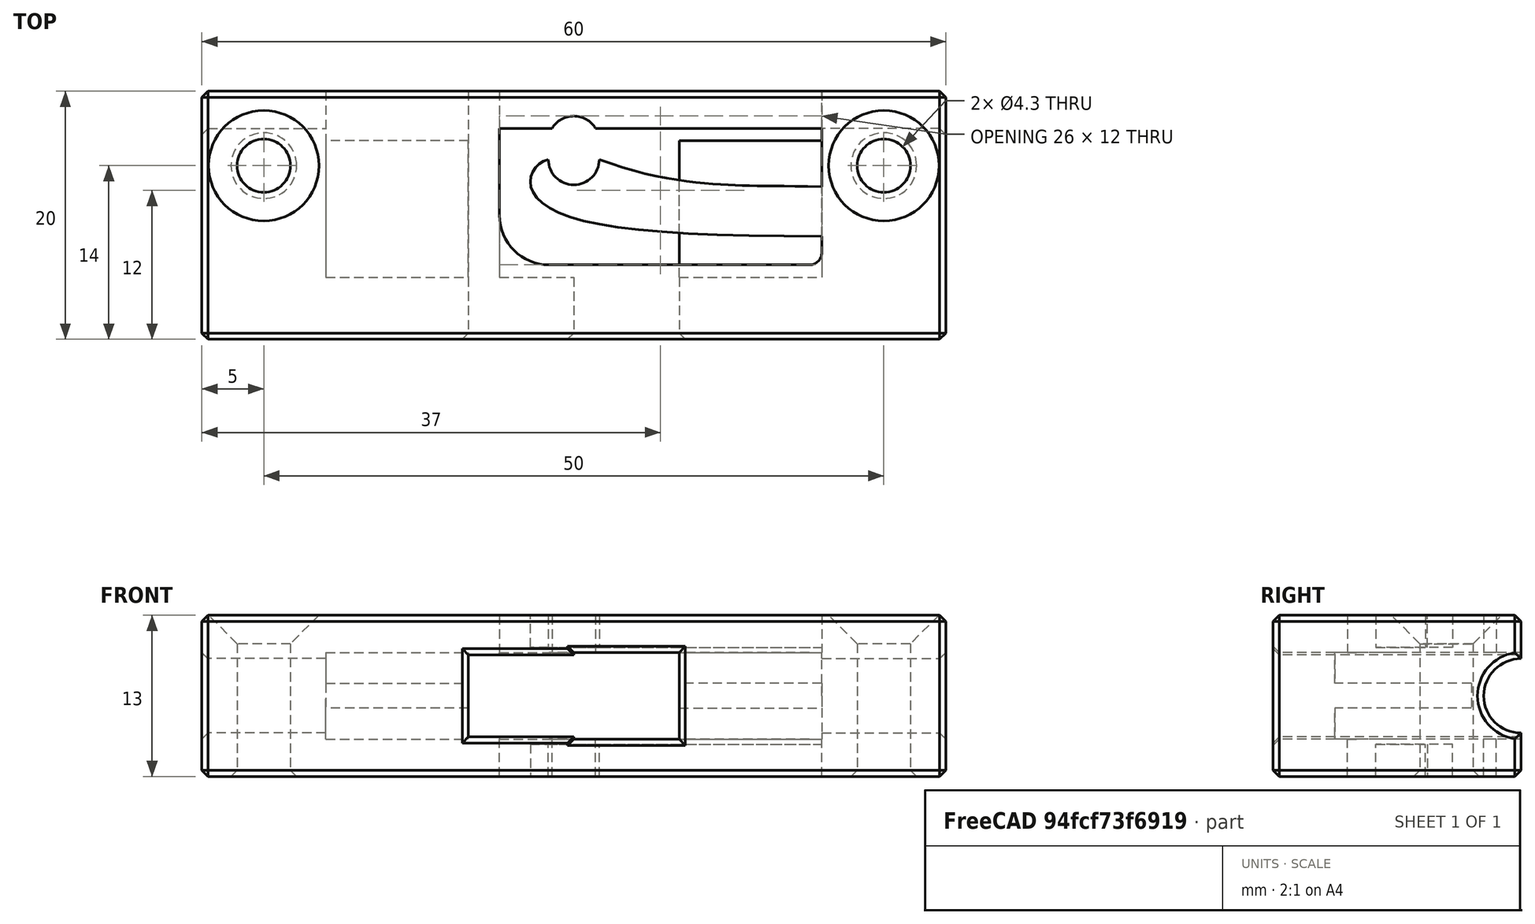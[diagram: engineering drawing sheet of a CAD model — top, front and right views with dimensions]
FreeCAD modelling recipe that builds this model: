
FCSTD DOCUMENT  (FreeCAD 1.1R20260414 (Git shallow))
Label: 01_hanger
License: All rights reserved
LicenseURL: http://en.wikipedia.org/wiki/All_rights_reserved
objects: Sketcher::SketchObject×8, PartDesign::Pocket×6, TechDraw::DrawProjGroupItem×6, PartDesign::Pad×2, PartDesign::Chamfer×2, TechDraw::DrawViewDimension×2, TechDraw::DrawSVGTemplate×1, PartDesign::Mirrored×1, App::Point×1, PartDesign::Body×1, TechDraw::DrawProjGroup×1, TechDraw::DrawViewSection×1, TechDraw::DrawPage×1
note: 52 computed .brp shape members not serialized (recipe doc carries the construction recipe); baked Part::Feature solids carry a one-line shape summary decoded from their .brp

FEATURE [Sketcher::SketchObject] Sketch
  ArcFitTolerance = 1e-06
  AttachmentSupport = -> [XY_Plane]
  ExternalTypes = [0]
  FullyConstrained = true
  MakeInternals = false
  MapMode = 5
  _ExternalGeoVersion = 0
  sketch-geometry (5):
    g0: LineSegment StartX=-30 StartY=10 StartZ=0 EndX=-30 EndY=-10 EndZ=0
    g1: LineSegment StartX=-30 StartY=-10 StartZ=0 EndX=30 EndY=-10 EndZ=0
    g2: LineSegment StartX=30 StartY=-10 StartZ=0 EndX=30 EndY=10 EndZ=0
    g3: LineSegment StartX=30 StartY=10 StartZ=0 EndX=-30 EndY=10 EndZ=0
    g4: LineSegment [constr] StartX=-30 StartY=10 StartZ=0 EndX=30 EndY=-10 EndZ=0
  constraints (13):
    c: Coincident(g0,g1)
    c: Coincident(g1,g2)
    c: Coincident(g2,g3)
    c: Coincident(g3,g0)
    c: Vertical(g0)
    c: Vertical(g2)
    c: Horizontal(g1)
    c: Horizontal(g3)
    c: Coincident(g4,g0)
    c: Coincident(g4,g1)
    c: Symmetric(g4,g4,g-1)
    c: DistanceX(g3,g3) = 60
    c: DistanceY(g0,g0) = 20
FEATURE [PartDesign::Pad] Pad
  Direction = (0,0,1)
  Length = 6.5
  Length2 = 10
  Profile = -> Sketch
  ReferenceAxis = -> Sketch [N_Axis]
  SideType = 0
  Suppressed = false
  Type = 0
  Type2 = 0
FEATURE [Sketcher::SketchObject] Sketch001
  ArcFitTolerance = 1e-06
  AttachmentSupport = -> [YZ_Plane]
  ExternalGeometry = -> [Pad]
  ExternalTypes = [0]
  FullyConstrained = true
  MakeInternals = false
  MapMode = 5
  Placement = pos=(0,0,0) rot=(0.57735,0.57735,0.57735;2.0944rad)
  _ExternalGeoVersion = 0
  sketch-geometry (3):
    g0: ArcOfCircle CenterX=10 CenterY=0 CenterZ=0 NormalX=0 NormalY=0 NormalZ=1 AngleXU=0 Radius=3 StartAngle=1.5708 EndAngle=3.14159
    g1: LineSegment StartX=7 StartY=4e-16 StartZ=0 EndX=10 EndY=0 EndZ=0
    g2: LineSegment StartX=10 StartY=0 StartZ=0 EndX=10 EndY=3 EndZ=0
  constraints (8):
    c: Coincident(g0,g-4)
    c: PointOnObject(g0,g-4)
    c: PointOnObject(g0,g-3)
    c: Radius(g0) = 3
    c: Coincident(g1,g0)
    c: Coincident(g1,g0)
    c: Coincident(g2,g0)
    c: Coincident(g2,g0)
FEATURE [PartDesign::Pocket] Pocket
  BaseFeature = -> Pad
  Direction = (-1,0,0)
  Length = 5
  Length2 = 5
  Profile = -> Sketch001
  ReferenceAxis = -> Sketch001 [N_Axis]
  SideType = 2
  Suppressed = false
  Type = 1
  Type2 = 0
FEATURE [Sketcher::SketchObject] Sketch002
  ArcFitTolerance = 1e-06
  AttachmentSupport = -> [XY_Plane]
  ExternalTypes = [0]
  FullyConstrained = true
  MakeInternals = false
  MapMode = 5
  _ExternalGeoVersion = 0
  sketch-geometry (4):
    g0: Circle CenterX=0 CenterY=5.95 CenterZ=0 NormalX=0 NormalY=0 NormalZ=1 AngleXU=0 Radius=2.05
    g1: LineSegment [constr] StartX=25 StartY=4 StartZ=0 EndX=-25 EndY=4 EndZ=0
    g2: Circle CenterX=25 CenterY=4 CenterZ=0 NormalX=0 NormalY=0 NormalZ=1 AngleXU=0 Radius=2.15
    g3: Circle CenterX=-25 CenterY=4 CenterZ=0 NormalX=0 NormalY=0 NormalZ=1 AngleXU=0 Radius=2.15
  constraints (11):
    c: PointOnObject(g0,g-2)
    c: Diameter(g0) = 4.1
    c: Distance(g0,g-3) = 4.05
    c: Horizontal(g1)
    c: Coincident(g2,g1)
    c: Coincident(g3,g1)
    c: Diameter(g2) = 4.3
    c: Diameter(g3) = 4.3
    c: DistanceX(g1,g1) = 50
    c: Distance(g1,g-3) = 6
    c: DistanceX(g-3,g1) = 5
FEATURE [PartDesign::Pocket] Pocket001
  BaseFeature = -> Pocket
  Direction = (0,0,-1)
  Length = 5
  Length2 = 5
  Profile = -> Sketch002
  ReferenceAxis = -> Sketch002 [N_Axis]
  SideType = 2
  Suppressed = false
  Type = 1
  Type2 = 0
FEATURE [Sketcher::SketchObject] Sketch003
  ArcFitTolerance = 1e-06
  AttachmentOffset = pos=(0,0,6.5) rot=(0,0,1;0rad)
  AttachmentSupport = -> [XY_Plane]
  ExternalGeometry = -> [Pocket001]
  ExternalTypes = [0]
  FullyConstrained = true
  MakeInternals = false
  MapMode = 5
  Placement = pos=(0,0,6.5) rot=(0,0,1;0rad)
  _ExternalGeoVersion = 0
  sketch-geometry (8):
    g0: LineSegment StartX=20 StartY=7 StartZ=0 EndX=-6 EndY=7 EndZ=0
    g1: LineSegment StartX=-6 StartY=7 StartZ=0 EndX=-6 EndY=0 EndZ=0
    g2: LineSegment StartX=-2 StartY=-4 StartZ=0 EndX=19 EndY=-4 EndZ=0
    g3: LineSegment StartX=20 StartY=-3 StartZ=0 EndX=20 EndY=7 EndZ=0
    g4: ArcOfCircle CenterX=-2 CenterY=-6e-16 CenterZ=0 NormalX=0 NormalY=0 NormalZ=1 AngleXU=0 Radius=4 StartAngle=3.14159 EndAngle=4.71239
    g5: GeomPoint [constr] X=-6 Y=-4 Z=0
    g6: ArcOfCircle CenterX=19 CenterY=-3 CenterZ=0 NormalX=0 NormalY=0 NormalZ=1 AngleXU=0 Radius=1 StartAngle=4.71239 EndAngle=6.28319
    g7: GeomPoint [constr] X=20 Y=-4 Z=0
  constraints (20):
    c: Coincident(g0,g1)
    c: Coincident(g3,g0)
    c: Horizontal(g0)
    c: Horizontal(g2)
    c: Vertical(g1)
    c: Vertical(g3)
    c: Distance(g7,g-3) = 10
    c: Distance(g-4,g0) = 3
    c: DistanceY(g5,g1) = 11
    c: PointOnObject(g5,g2)
    c: PointOnObject(g5,g1)
    c: Tangent(g2,g4) = -1.5708
    c: Tangent(g1,g4) = -1.5708
    c: Radius(g4) = 4
    c: DistanceX(g0,g0) = 26
    c: PointOnObject(g7,g2)
    c: PointOnObject(g7,g3)
    c: Tangent(g2,g6) = -1.5708
    c: Tangent(g3,g6) = -1.5708
    c: Radius(g6) = 1
FEATURE [PartDesign::Pocket] Pocket002
  BaseFeature = -> Pocket001
  Direction = (0,0,-1)
  Length = 4
  Length2 = 5
  Profile = -> Sketch003
  ReferenceAxis = -> Sketch003 [N_Axis]
  SideType = 0
  Suppressed = false
  Type = 0
  Type2 = 0
FEATURE [Sketcher::SketchObject] Sketch004
  ArcFitTolerance = 1e-06
  AttachmentOffset = pos=(0,0,-10) rot=(0,0,1;0rad)
  AttachmentSupport = -> [XZ_Plane]
  ExternalGeometry = -> [Pocket002]
  ExternalTypes = [0]
  FullyConstrained = false
  MakeInternals = false
  MapMode = 5
  Placement = pos=(0,10,-2.2e-15) rot=(1,0,0;1.5708rad)
  _ExternalGeoVersion = 0
  sketch-geometry (8):
    g0: LineSegment StartX=-20 StartY=1 StartZ=0 EndX=20 EndY=1 EndZ=0
    g1: LineSegment StartX=20 StartY=1 StartZ=0 EndX=20 EndY=3.5 EndZ=0
    g2: LineSegment StartX=-20 StartY=3.5 StartZ=0 EndX=-20 EndY=1 EndZ=0
    g3: LineSegment StartX=-20 StartY=3.5 StartZ=0 EndX=-8.5 EndY=3.5 EndZ=0
    g4: LineSegment StartX=-8.5 StartY=3.5 StartZ=0 EndX=-8.5 EndY=3.3 EndZ=0
    g5: LineSegment StartX=-8.5 StartY=3.3 StartZ=0 EndX=-6 EndY=3.3 EndZ=0
    g6: LineSegment StartX=-6 StartY=3.3 StartZ=0 EndX=-6 EndY=3.5 EndZ=0
    g7: LineSegment StartX=-6 StartY=3.5 StartZ=0 EndX=20 EndY=3.5 EndZ=0
  constraints (23):
    c: Coincident(g0,g1)
    c: Coincident(g2,g0)
    c: Horizontal(g0)
    c: Vertical(g1)
    c: Vertical(g2)
    c: DistanceX(g0,g0) = 40
    c: Coincident(g3,g2)
    c: Horizontal(g3)
    c: Coincident(g4,g3)
    c: Coincident(g5,g4)
    c: Vertical(g4)
    c: Horizontal(g5)
    c: Coincident(g6,g5)
    c: Vertical(g6)
    c: Coincident(g7,g6)
    c: Coincident(g7,g1)
    c: Horizontal(g7)
    c: Equal(g4,g6)
    c: Distance(g4,g4) = 0.2
    c: Distance(g1,g1) = 2.5
    c: Distance(g0,g-2) = 20
    c: DistanceX(g2,g3) = 11.5
    c: Distance(g5,g5) = 2.5
FEATURE [PartDesign::Pocket] Pocket003
  BaseFeature = -> Pocket002
  Direction = (0,1,-2e-16)
  Length = 15
  Length2 = 5
  Profile = -> Sketch004
  ReferenceAxis = -> Sketch004 [N_Axis]
  Reversed = true
  SideType = 0
  Suppressed = false
  Type = 0
  Type2 = 0
FEATURE [Sketcher::SketchObject] Sketch005
  ArcFitTolerance = 1e-06
  AttachmentSupport = -> [XZ_Plane]
  ExternalTypes = [0]
  FullyConstrained = true
  MakeInternals = false
  MapMode = 5
  Placement = pos=(0,0,0) rot=(1,0,0;1.5708rad)
  _ExternalGeoVersion = 0
  sketch-geometry (6):
    g0: LineSegment StartX=-8.5 StartY=3.3 StartZ=0 EndX=-8.5 EndY=0 EndZ=0
    g1: LineSegment StartX=-8.5 StartY=0 StartZ=0 EndX=8.5 EndY=0 EndZ=0
    g2: LineSegment StartX=8.5 StartY=0 StartZ=0 EndX=8.5 EndY=3.5 EndZ=0
    g3: LineSegment StartX=8.5 StartY=3.5 StartZ=0 EndX=0 EndY=3.5 EndZ=0
    g4: LineSegment StartX=0 StartY=3.5 StartZ=0 EndX=0 EndY=3.3 EndZ=0
    g5: LineSegment StartX=-8.5 StartY=3.3 StartZ=0 EndX=0 EndY=3.3 EndZ=0
  constraints (18):
    c: Coincident(g0,g1)
    c: Coincident(g1,g2)
    c: Coincident(g2,g3)
    c: Vertical(g0)
    c: Vertical(g2)
    c: Horizontal(g1)
    c: Horizontal(g3)
    c: PointOnObject(g1,g-1)
    c: Distance(g-1,g2) = 8.5
    c: Distance(g2,g2) = 3.5
    c: Coincident(g5,g4)
    c: Horizontal(g5)
    c: Coincident(g0,g5)
    c: PointOnObject(g4,g-2)
    c: Distance(g-2,g0) = 8.5
    c: Coincident(g4,g3)
    c: Distance(g3,g5) = 0.2
    c: Vertical(g4)
FEATURE [PartDesign::Pocket] Pocket004
  BaseFeature = -> Pocket003
  Direction = (0,1,-2e-16)
  Length = 5
  Length2 = 5
  Profile = -> Sketch005
  ReferenceAxis = -> Sketch005 [N_Axis]
  SideType = 2
  Suppressed = false
  Type = 1
  Type2 = 0
FEATURE [Sketcher::SketchObject] Sketch006
  ArcFitTolerance = 1e-06
  AttachmentOffset = pos=(0,0,6.5) rot=(0,0,1;0rad)
  AttachmentSupport = -> [XY_Plane]
  ExternalGeometry = -> [Pocket004]
  ExternalTypes = [0]
  FullyConstrained = false
  MakeInternals = false
  MapMode = 5
  Placement = pos=(0,0,6.5) rot=(0,0,1;0rad)
  _ExternalGeoVersion = 0
  sketch-geometry (20):
    g0: ArcOfCircle CenterX=0 CenterY=4.5 CenterZ=0 NormalX=0 NormalY=0 NormalZ=1 AngleXU=0 Radius=2.05 StartAngle=3.14159 EndAngle=6.28319
    g1: LineSegment [constr] StartX=-2.05 StartY=4.5 StartZ=0 EndX=2.05 EndY=4.5 EndZ=0
    g2-g5: Circle [constr] x4 (B-spline internal-alignment scaffolding for g6; pole/knot coordinates omitted)
    g6: BSplineCurve PolesCount=5 KnotsCount=2 Degree=4 IsPeriodic=0
    g7: GeomPoint [constr] X=-2.05 Y=4.5 Z=0
    g8: GeomPoint [constr] X=20 Y=-1.7 Z=0
    g9-g13: Circle [constr] x5 (B-spline internal-alignment scaffolding for g14; pole/knot coordinates omitted)
    g14: BSplineCurve PolesCount=5 KnotsCount=3 Degree=3 IsPeriodic=0
    g15: GeomPoint [constr] X=2.05 Y=4.5 Z=0
    g16: GeomPoint [constr] X=11.5418 Y=2.50077 Z=0
    g17: GeomPoint [constr] X=20 Y=2.3 Z=0
    g18: Circle [constr] CenterX=20 CenterY=-1.7 CenterZ=0 NormalX=0 NormalY=0 NormalZ=1 AngleXU=0 Radius=1
    g19: LineSegment StartX=20 StartY=-1.7 StartZ=0 EndX=20 EndY=2.3 EndZ=0
  constraints (30):
    c: PointOnObject(g0,g-2)
    c: Diameter(g0) = 4.1
    c: Distance(g0,g-4) = 5.5
    c: Horizontal(g1)
    c: PointOnObject(g0,g1)
    c: Coincident(g0,g1)
    c: Coincident(g0,g1)
    c: PointOnObject(g13,g-3)
    c: Weight(g2) = 1
    c: Equal(g2,g3)
    c: Equal(g2,g4)
    c: Equal(g2,g5)
    c: InternalAlignment(g2-g5 -> g6) x4
    c: InternalAlignment(g7,g6)
    c: InternalAlignment(g8,g6)
    c: Weight(g9) = 1
    c: Equal(g9, g10-g13) x4
    c: InternalAlignment(g9-g13 -> g14) x5
    c: InternalAlignment(g15,g14)
    c: InternalAlignment(g16,g14)
    c: InternalAlignment(g17,g14)
    c: Coincident(g9,g0)
    c: Coincident(g6,g0)
    c: PointOnObject(g6,g-3)
    c: DistanceY(g6,g14) = 4
    c: Distance(g6,g-5) = 2.3
    c: InternalAlignment(g18,g6)
    c: Equal(g18,g2)
    c: Coincident(g19,g6)
    c: Coincident(g19,g14)
FEATURE [PartDesign::Pad] Pad001
  BaseFeature = -> Pocket004
  Direction = (0,0,1)
  Length = 2.6
  Length2 = 10
  Profile = -> Sketch006
  ReferenceAxis = -> Sketch006 [N_Axis]
  Refine = true
  Reversed = true
  SideType = 0
  Suppressed = false
  Type = 0
  Type2 = 0
FEATURE [TechDraw::DrawSVGTemplate] Template
  Height = 210
  Orientation = 1
  Template = C:/Program Files/FreeCAD 1.0/data/Mod/TechDraw/Templates/Default_Template_A4_Landscape.svg
  Width = 297
FEATURE [Sketcher::SketchObject] Sketch007
  ArcFitTolerance = 1e-06
  AttachmentOffset = pos=(0,0,-10) rot=(0,0,1;0rad)
  AttachmentSupport = -> [XZ_Plane]
  ExternalGeometry = -> [Pad001]
  ExternalTypes = [0]
  FullyConstrained = true
  MakeInternals = false
  MapMode = 5
  Placement = pos=(0,10,-2.2e-15) rot=(1,0,0;1.5708rad)
  _ExternalGeoVersion = 0
  sketch-geometry (4):
    g0: LineSegment StartX=-20 StartY=3 StartZ=0 EndX=-20 EndY=1.8e-15 EndZ=0
    g1: LineSegment StartX=-20 StartY=1.8e-15 StartZ=0 EndX=20 EndY=1.8e-15 EndZ=0
    g2: LineSegment StartX=20 StartY=1.8e-15 StartZ=0 EndX=20 EndY=3 EndZ=0
    g3: LineSegment StartX=20 StartY=3 StartZ=0 EndX=-20 EndY=3 EndZ=0
  constraints (11):
    c: Coincident(g0,g1)
    c: Coincident(g1,g2)
    c: Coincident(g2,g3)
    c: Coincident(g3,g0)
    c: Vertical(g0)
    c: Vertical(g2)
    c: Horizontal(g1)
    c: Horizontal(g3)
    c: Coincident(g0,g-3)
    c: DistanceX(g3,g3) = 40
    c: DistanceY(g0,g0) = 3
FEATURE [PartDesign::Pocket] Pocket005
  BaseFeature = -> Pad001
  Direction = (0,1,-2e-16)
  Length = 4
  Length2 = 5
  Profile = -> Sketch007
  ReferenceAxis = -> Sketch007 [N_Axis]
  Reversed = true
  SideType = 0
  Suppressed = false
  Type = 0
  Type2 = 0
FEATURE [PartDesign::Mirrored] Mirrored
  BaseFeature = -> Pocket005
  MirrorPlane = -> XY_Plane
  Refine = true
  Suppressed = false
  TransformMode = 1
FEATURE [PartDesign::Chamfer] Chamfer001
  Angle = 45
  Base = -> Mirrored [Edge108,Edge107]
  BaseFeature = -> Mirrored
  ChamferType = 0
  FlipDirection = false
  Size = 2.3
  Size2 = 1
  SupportTransform = false
  Suppressed = false
  UseAllEdges = false
FEATURE [App::Point] Origin001  label="Origin"
  Role = Origin
FEATURE [PartDesign::Chamfer] Chamfer
  Angle = 45
  Base = -> Chamfer001 [Edge2,Edge5,Edge3,Edge4,Edge28,Edge27,Edge25,Edge39,Edge114,Edge24,Edge126,Edge102,Edge21,Edge37,Edge40,Edge38,Edge26,Edge23,Edge29,Edge31,Edge32,Edge33,Edge34,Edge35,Edge36,Edge30]
  BaseFeature = -> Chamfer001
  ChamferType = 0
  FlipDirection = false
  Refine = true
  Size = 0.5
  Size2 = 1
  SupportTransform = false
  Suppressed = false
  UseAllEdges = false
FEATURE [PartDesign::Body] Body
  AllowCompound = false
  Group = -> [Sketch,Pad,Sketch001,Pocket,Sketch002,Pocket001,Sketch003,Pocket002,Sketch004,Pocket003,Sketch005,Pocket004,Sketch006,Pad001,Sketch007,Pocket005,Mirrored,Chamfer001,Chamfer]
  Origin = -> Origin
  Tip = -> Chamfer
FEATURE [TechDraw::DrawProjGroupItem] View  label="Front"
  CoarseView = false
  Direction = (0,-1,0)
  Focus = 100
  HardHidden = false
  IsoCount = 0
  IsoHidden = false
  IsoVisible = false
  LockPosition = true
  Perspective = false
  Rotation = 0
  RotationVector = (1,0,0)
  ScaleType = 2
  ScrubCount = 1
  SeamHidden = false
  SeamVisible = true
  SmoothHidden = false
  SmoothVisible = true
  Source = -> [Body]
  Type = 0
  X = 0
  XDirection = (1,0,0)
  Y = 0
FEATURE [TechDraw::DrawProjGroupItem] ProjItem  label="Right"
  CoarseView = false
  Direction = (1,-1e-16,0)
  Focus = 100
  HardHidden = false
  IsoCount = 0
  IsoHidden = false
  IsoVisible = false
  LockPosition = false
  Perspective = false
  Rotation = 0
  RotationVector = (1,0,0)
  ScaleType = 0
  ScrubCount = 1
  SeamHidden = false
  SeamVisible = true
  SmoothHidden = false
  SmoothVisible = true
  Source = -> [Body]
  Type = 2
  X = 55
  XDirection = (1e-16,1,0)
  Y = 0
FEATURE [TechDraw::DrawProjGroupItem] ProjItem001  label="Left"
  CoarseView = false
  Direction = (-1,-1e-16,0)
  Focus = 100
  HardHidden = false
  IsoCount = 0
  IsoHidden = false
  IsoVisible = false
  LockPosition = false
  Perspective = false
  Rotation = 0
  RotationVector = (1,0,0)
  ScaleType = 0
  ScrubCount = 1
  SeamHidden = false
  SeamVisible = true
  SmoothHidden = false
  SmoothVisible = true
  Source = -> [Body]
  Type = 1
  X = -55
  XDirection = (1e-16,-1,0)
  Y = 0
FEATURE [TechDraw::DrawProjGroupItem] ProjItem002  label="Bottom"
  CoarseView = false
  Direction = (0,0,-1)
  Focus = 100
  HardHidden = false
  IsoCount = 0
  IsoHidden = false
  IsoVisible = false
  LockPosition = false
  Perspective = false
  Rotation = 0
  RotationVector = (1,0,0)
  ScaleType = 0
  ScrubCount = 1
  SeamHidden = false
  SeamVisible = true
  SmoothHidden = false
  SmoothVisible = true
  Source = -> [Body]
  Type = 5
  X = 0
  XDirection = (1,0,0)
  Y = -31.5
FEATURE [TechDraw::DrawProjGroupItem] ProjItem003  label="Top"
  CoarseView = false
  Direction = (0,0,1)
  Focus = 100
  HardHidden = false
  IsoCount = 0
  IsoHidden = false
  IsoVisible = false
  LockPosition = false
  Perspective = false
  Rotation = 0
  RotationVector = (1,0,0)
  ScaleType = 0
  ScrubCount = 1
  SeamHidden = false
  SeamVisible = true
  SmoothHidden = false
  SmoothVisible = true
  Source = -> [Body]
  Type = 4
  X = 0
  XDirection = (1,0,0)
  Y = 31.5
FEATURE [TechDraw::DrawViewDimension] Dimension
  AngleOverride = false
  Arbitrary = false
  ArbitraryTolerances = false
  BoxCorners = (2) [(-30,-3.25,0),(30,3.25,0)]
  EqualTolerance = true
  ExtensionAngle = 0
  FormatSpec = %.2w
  FormatSpecOverTolerance = %+.2w
  FormatSpecUnderTolerance = %+.2w
  Inverted = false
  LineAngle = 0
  LockPosition = false
  MeasureType = 1
  OverTolerance = 0
  References2D = -> [View]
  Rotation = 0
  ScaleType = 0
  ShowUnits = false
  TheoreticalExact = false
  Type = 1
  UnderTolerance = 0
  UseActualArea = true
  X = 4.15098
  Y = -1.02237
FEATURE [TechDraw::DrawProjGroupItem] ProjItem004  label="Rear"
  CoarseView = false
  Direction = (0,1,0)
  Focus = 100
  HardHidden = false
  IsoCount = 0
  IsoHidden = false
  IsoVisible = false
  LockPosition = false
  Perspective = false
  Rotation = 0
  RotationVector = (1,0,0)
  ScaleType = 0
  ScrubCount = 1
  SeamHidden = false
  SeamVisible = true
  SmoothHidden = false
  SmoothVisible = true
  Source = -> [Body]
  Type = 3
  X = 110
  XDirection = (-1,0,0)
  Y = 0
FEATURE [TechDraw::DrawProjGroup] ProjGroup
  Anchor = -> View
  AutoDistribute = true
  LockPosition = false
  ProjectionType = 1
  Rotation = 0
  ScaleType = 0
  Source = -> [Body]
  Views = -> [View,ProjItem,ProjItem001,ProjItem002,ProjItem003,ProjItem004]
  X = 148.5
  Y = 105
  spacingX = 15
  spacingY = 15
FEATURE [TechDraw::DrawViewSection] SectionView  label="Section  - "
  BaseView = -> ProjItem003
  CoarseView = false
  CutSurfaceDisplay = 2
  Direction = (1,0,0)
  FileGeomPattern = <path>
  FileHatchPattern = <path>
  Focus = 100
  FuseBeforeCut = false
  HardHidden = false
  HatchOffset = (0,0,0)
  HatchRotation = 0
  HatchScale = 1
  IsoCount = 0
  IsoHidden = false
  IsoVisible = false
  LockPosition = false
  NameGeomPattern = Diamond
  Perspective = false
  Rotation = 90
  ScaleType = 0
  ScrubCount = 1
  SeamHidden = false
  SeamVisible = false
  SectionDirection = 4
  SectionLineStretch = 1
  SectionNormal = (1,0,0)
  SectionOrigin = (-25,0,0)
  SmoothHidden = false
  SmoothVisible = true
  Source = -> [Body]
  TrimAfterCut = false
  UsePreviousCut = false
  X = 86.526
  XDirection = (0,1,0)
  Y = 148.746
FEATURE [TechDraw::DrawViewDimension] Dimension001
  AngleOverride = false
  Arbitrary = false
  ArbitraryTolerances = false
  BoxCorners = (2) [(-6.5,-10,-1e-07),(6.5,10,1e-07)]
  EqualTolerance = true
  ExtensionAngle = 0
  FormatSpec = %.2w
  FormatSpecOverTolerance = %+.2w
  FormatSpecUnderTolerance = %+.2w
  Inverted = false
  LineAngle = 0
  LockPosition = false
  MeasureType = 1
  OverTolerance = 0
  References2D = -> [SectionView]
  Rotation = 0
  ScaleType = 0
  ShowUnits = false
  TheoreticalExact = false
  Type = 0
  UnderTolerance = 0
  UseActualArea = true
  X = 17.0696
  Y = 13.5367
FEATURE [TechDraw::DrawPage] Page
  KeepUpdated = true
  NextBalloonIndex = 1
  ProjectionType = 0
  Template = -> Template
  Views = -> [ProjGroup,Dimension,SectionView,Dimension001]
note: 2 file-system paths scrubbed to <path> (originals preserved in the JSON sidecar)
